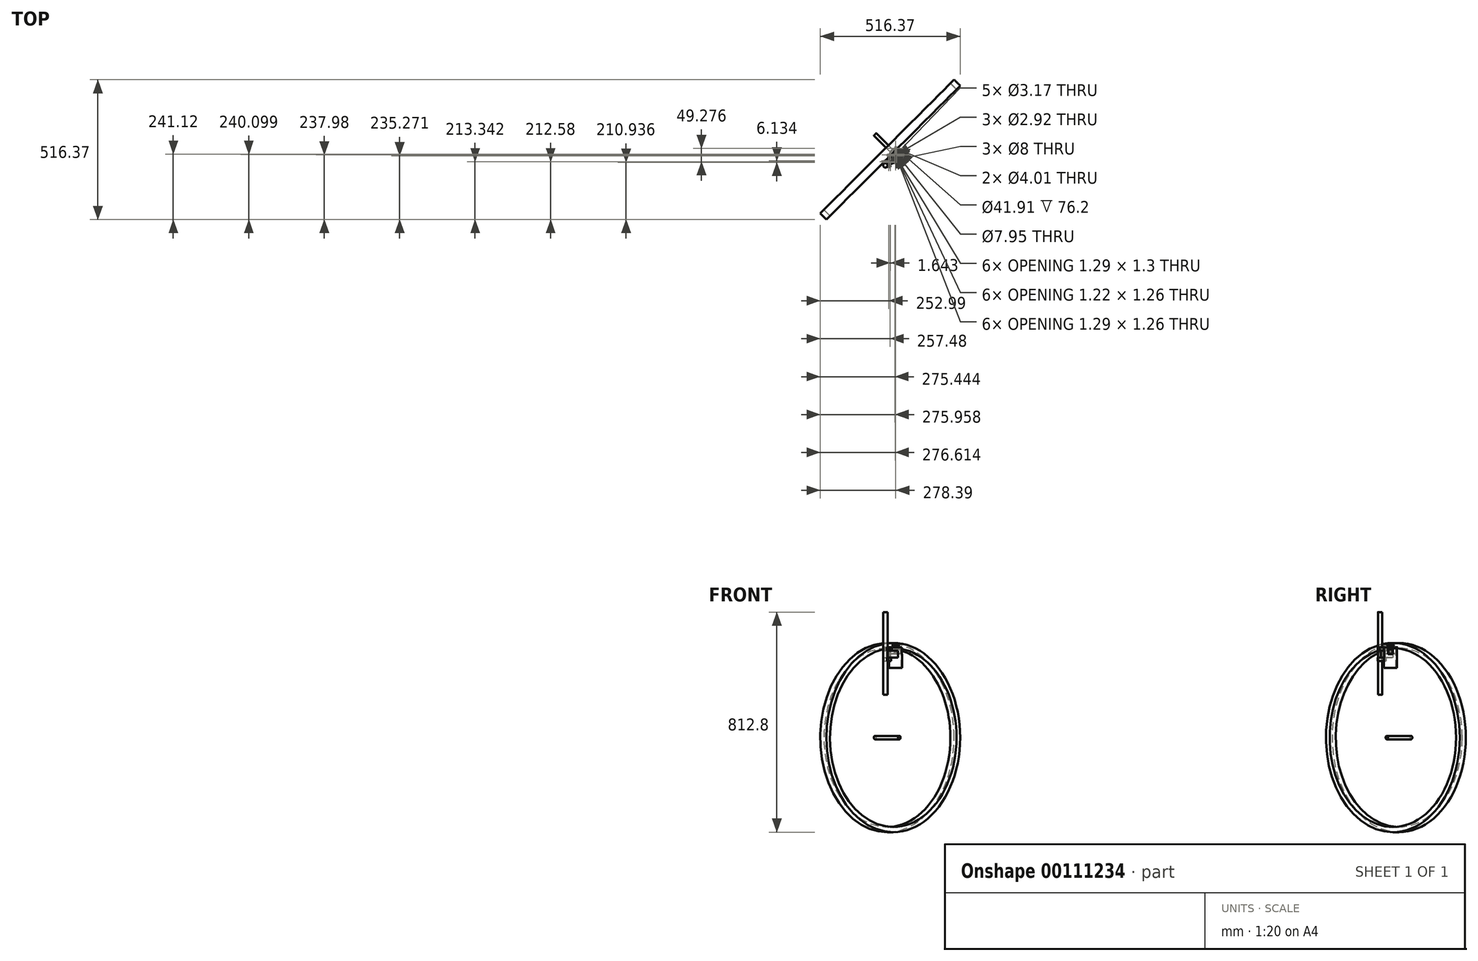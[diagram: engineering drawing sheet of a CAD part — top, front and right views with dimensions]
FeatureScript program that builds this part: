
annotation { "Feature Type Name" : "Feature", "Feature Type Description" : "" }
export const myFeature = defineFeature(function(context is Context, id is Id, definition is map)
    precondition{}
    {
        {
            var Q0;
            Q0=qCreatedBy(makeId("Top.planeOp"),FACE);
            var sketch = newSketch(context, id + "F0", { "sketchPlane" : qUnion([Q0])});
            skCircle(sketch, "E0", {"center": v(0, 0) * mm, "radius": 20.96 * mm});
            skSolve(sketch);
        }
        {
            var Q0;
            Q0=makeQuery(id+"F0.imprint","IMPRINT",FACE,{"disambiguationData":[TD([[makeQuery(id+"F0.imprint","IMPRINT",EDGE,{"derivedFrom":sQuery(id+"F0.wireOp",EDGE,"E0")}),1.0]])]});
            extrude(context, id + "F1", {"entities" : qUnion([Q0]), "depth" : 21.74 * mm});
        }
        {
            var Q0;
            Q0=makeQuery(id+"F1.opExtrude","CAP_FACE",FACE,{"disambiguationData":[OSD([sQuery(id+"F0.wireOp",EDGE,"E0")])],"isStart":false});
            var sketch = newSketch(context, id + "F2", { "sketchPlane" : qUnion([Q0])});
            skArc(sketch, "E1.0", {"start": v(15.25, -13.43) * mm, "mid": v(20.32, 0) * mm, "end": v(15.25, 13.43) * mm});
            skLineSegment(sketch, "E2", {"start": v(0, 32.45) * mm, "end": v(0, -32.45) * mm, "construction": true});
            skLineSegment(sketch, "E3", {"start": v(0, 0) * mm, "end": v(29.8, 0) * mm, "construction": true});
            skCircle(sketch, "E4", {"center": v(0, 24.64) * mm, "radius": 2 * mm});
            skCircle(sketch, "E5", {"center": v(0, -24.64) * mm, "radius": 2 * mm});
            skArc(sketch, "E6.0", {"start": v(3.03, 27.3) * mm, "mid": v(0, 28.68) * mm, "end": v(-3.03, 27.3) * mm});
            skArc(sketch, "E7", {"start": v(-3.03, -27.3) * mm, "mid": v(0, -28.68) * mm, "end": v(3.03, -27.3) * mm});
            skLineSegment(sketch, "E8", {"start": v(-3.03, 27.3) * mm, "end": v(-15.25, 13.43) * mm});
            skLineSegment(sketch, "E9", {"start": v(3.03, 27.3) * mm, "end": v(15.25, 13.43) * mm});
            skLineSegment(sketch, "E10", {"start": v(-3.03, -27.3) * mm, "end": v(-15.25, -13.43) * mm});
            skLineSegment(sketch, "E11", {"start": v(3.03, -27.3) * mm, "end": v(15.25, -13.43) * mm});
            skArc(sketch, "E12.trimOffspring", {"start": v(-15.25, 13.43) * mm, "mid": v(-20.32, 0) * mm, "end": v(-15.25, -13.43) * mm});
            skSolve(sketch);
        }
        {
            var Q0;
            Q0=makeQuery(id+"F2.imprint","IMPRINT",FACE,{"disambiguationData":[TD([[makeQuery(id+"F2.imprint","IMPRINT",EDGE,{"derivedFrom":sQuery(id+"F2.wireOp",EDGE,"E4")}),-1.0]])]});
            var Q1;
            {var subQ8=sQuery(id+"F2.wireOp",EDGE,"E1.0");Q1=makeQuery(id+"F2.imprint","IMPRINT",FACE,{"disambiguationData":[TD([[makeQuery(id+"F2.imprint","IMPRINT",EDGE,{"derivedFrom":subQ8}),1.0]])]});}
            var Q2;
            Q2=makeQuery(id+"F2.imprint","IMPRINT",FACE,{"disambiguationData":[TD([[makeQuery(id+"F2.imprint","IMPRINT",EDGE,{"derivedFrom":sQuery(id+"F2.wireOp",EDGE,"E5")}),-1.0]])]});
            extrude(context, id + "F3", {"entities" : qUnion([Q0, Q1, Q2]), "depth" : 0.76 * mm});
        }
        {
            var Q0;
            Q0=makeQuery(id+"F3.opExtrude","CAP_FACE",FACE,{"disambiguationData":[OSD([sQuery(id+"F2.wireOp",EDGE,"E1.0"),sQuery(id+"F2.wireOp",EDGE,"E4"),sQuery(id+"F2.wireOp",EDGE,"E5"),sQuery(id+"F2.wireOp",EDGE,"E6.0"),sQuery(id+"F2.wireOp",EDGE,"E7"),sQuery(id+"F2.wireOp",EDGE,"E8"),sQuery(id+"F2.wireOp",EDGE,"E9"),sQuery(id+"F2.wireOp",EDGE,"E10"),sQuery(id+"F2.wireOp",EDGE,"E11"),sQuery(id+"F2.wireOp",EDGE,"E12.trimOffspring")])],"isStart":false});
            var sketch = newSketch(context, id + "F4", { "sketchPlane" : qUnion([Q0])});
            skCircle(sketch, "E13", {"center": v(0, 0) * mm, "radius": 4.94 * mm});
            skCircle(sketch, "E14", {"center": v(0, 0) * mm, "radius": 1.46 * mm});
            skSolve(sketch);
        }
        {
            var Q0;
            Q0=makeQuery(id+"F4.imprint","IMPRINT",FACE,{"disambiguationData":[TD([[makeQuery(id+"F4.imprint","IMPRINT",EDGE,{"derivedFrom":sQuery(id+"F4.wireOp",EDGE,"E13")}),1.0]])]});
            extrude(context, id + "F5", {"entities" : qUnion([Q0]), "operationType" : NewBodyOperationType.ADD, "depth" : 1.4 * mm});
        }
        {
            var Q0;
            Q0=makeQuery(id+"F4.imprint","IMPRINT",FACE,{"disambiguationData":[TD([[makeQuery(id+"F4.imprint","IMPRINT",EDGE,{"derivedFrom":sQuery(id+"F4.wireOp",EDGE,"E14")}),1.0]])]});
            extrude(context, id + "F6", {"entities" : qUnion([Q0]), "operationType" : NewBodyOperationType.REMOVE, "endBound" : BoundingType.THROUGH_ALL, "oppositeDirection" : true, "depth" : 25.4 * mm});
        }
        {
            var Q0;
            Q0=makeQuery(id+"F5.opExtrude","CAP_FACE",FACE,{"disambiguationData":[OSD([sQuery(id+"F4.wireOp",EDGE,"E13"),sQuery(id+"F4.wireOp",EDGE,"E14")])],"isStart":false});
            var sketch = newSketch(context, id + "F7", { "sketchPlane" : qUnion([Q0])});
            skCircle(sketch, "E15.0", {"center": v(0, 0) * mm, "radius": 1.46 * mm});
            skSolve(sketch);
        }
        {
            var Q0;
            Q0 = qSketchRegion(id + "F7", true);
            var Q1;
            Q1=makeQuery(id+"F7.imprint","IMPRINT",FACE,{"disambiguationData":[TD([[makeQuery(id+"F7.imprint","IMPRINT",EDGE,{"derivedFrom":sQuery(id+"F7.wireOp",EDGE,"E15.0")}),1.0]])]});
            extrude(context, id + "F8", {"entities" : qUnion([Q0, Q1]), "depth" : 7.62 * mm, "hasSecondDirection" : true, "secondDirectionOppositeDirection" : true, "secondDirectionDepth" : 25.65 * mm});
        }
        {
            var Q0;
            Q0=makeQuery(id+"F1.opExtrude","CAP_FACE",FACE,{"disambiguationData":[OSD([sQuery(id+"F0.wireOp",EDGE,"E0")])],"isStart":true});
            var sketch = newSketch(context, id + "F9", { "sketchPlane" : qUnion([Q0])});
            skCircle(sketch, "E16", {"center": v(0, 0) * mm, "radius": 15.58 * mm});
            skSolve(sketch);
        }
        {
            var Q0;
            Q0 = qSketchRegion(id + "F9", true);
            extrude(context, id + "F10", {"entities" : qUnion([Q0]), "depth" : 1.68 * mm});
        }
        {
            var Q0;
            Q0=makeQuery(id+"F1.opExtrude","CAP_EDGE",EDGE,{"disambiguationData":[OSD([sQuery(id+"F0.wireOp",EDGE,"E0")])],"isStart":false});
            fillet(context, id + "F11", {"entities" : qUnion([Q0]), "radius" : 0.25 * mm, "tangentPropagation" : true, "allowEdgeOverflow" : false});
        }
        {
            var Q0;
            Q0=makeQuery(id+"F8.opExtrude","CAP_FACE",FACE,{"disambiguationData":[OSD([sQuery(id+"F7.wireOp",EDGE,"E15.0")])],"isStart":false});
            var sketch = newSketch(context, id + "F12", { "sketchPlane" : qUnion([Q0])});
            skCircle(sketch, "E17", {"center": v(0, 0) * mm, "radius": 3.98 * mm});
            skCircle(sketch, "E18.0", {"center": v(0, 0) * mm, "radius": 1.46 * mm});
            skSolve(sketch);
        }
        {
            var Q0;
            Q0=makeQuery(id+"F12.imprint","IMPRINT",FACE,{"disambiguationData":[TD([[makeQuery(id+"F12.imprint","IMPRINT",EDGE,{"derivedFrom":sQuery(id+"F12.wireOp",EDGE,"E17")}),1.0]])]});
            extrude(context, id + "F13", {"entities" : qUnion([Q0]), "oppositeDirection" : true, "depth" : 6.1 * mm});
        }
        {
            var Q0;
            Q0=qCreatedBy(makeId("Right.planeOp"),FACE);
            cPlane(context, id + "F14", {"entities" : qUnion([Q0]), "cplaneType" : CPlaneType.OFFSET, "offset" : 21.34 * mm, "width" : 152.4 * mm, "height" : 152.4 * mm});
        }
        {
            var Q0;
            Q0=qCreatedBy(id+"F14.planeOp",FACE);
            var sketch = newSketch(context, id + "F15", { "sketchPlane" : qUnion([Q0])});
            skLineSegment(sketch, "E19.bottom", {"start": v(7.96, -1.7) * mm, "end": v(-7.96, -1.7) * mm});
            skLineSegment(sketch, "E19.top", {"start": v(7.96, 14.99) * mm, "end": v(-7.96, 14.99) * mm});
            skLineSegment(sketch, "E19.left", {"start": v(7.96, -1.7) * mm, "end": v(7.96, 14.99) * mm});
            skLineSegment(sketch, "E19.right", {"start": v(-7.96, -1.7) * mm, "end": v(-7.96, 14.99) * mm});
            skPoint(sketch, "E19.middle", {"position": v(0, 6.64) * mm});
            skSolve(sketch);
        }
        {
            var Q0;
            Q0=makeQuery(id+"F15.imprint","IMPRINT",FACE,{"disambiguationData":[TD([[makeQuery(id+"F15.imprint","IMPRINT",EDGE,{"derivedFrom":sQuery(id+"F15.wireOp",EDGE,"E19.bottom")}),-1.0]])]});
            extrude(context, id + "F16", {"entities" : qUnion([Q0]), "depth" : 0.91 * mm});
        }
        {
            var Q0;
            Q0=makeQuery(id+"F16.opExtrude","SWEPT_EDGE",EDGE,{"disambiguationData":[OSD([sQuery(id+"F15.wireOp",EDGE,"E19.top"),sQuery(id+"F15.wireOp",EDGE,"E19.right")])]});
            chamfer(context, id + "F17", {"entities" : qUnion([Q0]), "width" : 1.27 * mm, "tangentPropagation" : true});
        }
        {
            var Q0;
            Q0=makeQuery(id+"F3.opExtrude","CAP_FACE",FACE,{"disambiguationData":[OSD([sQuery(id+"F2.wireOp",EDGE,"E1.0"),sQuery(id+"F2.wireOp",EDGE,"E4"),sQuery(id+"F2.wireOp",EDGE,"E5"),sQuery(id+"F2.wireOp",EDGE,"E6.0"),sQuery(id+"F2.wireOp",EDGE,"E7"),sQuery(id+"F2.wireOp",EDGE,"E8"),sQuery(id+"F2.wireOp",EDGE,"E9"),sQuery(id+"F2.wireOp",EDGE,"E10"),sQuery(id+"F2.wireOp",EDGE,"E11"),sQuery(id+"F2.wireOp",EDGE,"E12.trimOffspring")])],"isStart":true});
            var sketch = newSketch(context, id + "F18", { "sketchPlane" : qUnion([Q0])});
            skCircle(sketch, "E20.0", {"center": v(0, 0) * mm, "radius": 20.96 * mm});
            skCircle(sketch, "E21", {"center": v(0, 0) * mm, "radius": 24.13 * mm});
            skSolve(sketch);
        }
        {
            var Q0;
            Q0 = qSketchRegion(id + "F18", true);
            extrude(context, id + "F19", {"entities" : qUnion([Q0]), "depth" : 76.2 * mm});
        }
        {
            var Q0;
            Q0=makeQuery(id+"F16.opExtrude","CAP_FACE",FACE,{"disambiguationData":[OSD([sQuery(id+"F15.wireOp",EDGE,"E19.bottom"),sQuery(id+"F15.wireOp",EDGE,"E19.top"),sQuery(id+"F15.wireOp",EDGE,"E19.left"),sQuery(id+"F15.wireOp",EDGE,"E19.right")])],"isStart":false});
            var sketch = newSketch(context, id + "F20", { "sketchPlane" : qUnion([Q0])});
            skLineSegment(sketch, "E22.0", {"start": v(7.96, 14.99) * mm, "end": v(-6.7, 14.99) * mm, "construction": true});
            skLineSegment(sketch, "E23.0", {"start": v(7.96, -1.7) * mm, "end": v(7.96, 14.99) * mm, "construction": true});
            skLineSegment(sketch, "E24.0", {"start": v(7.96, -1.7) * mm, "end": v(-7.96, -1.7) * mm, "construction": true});
            skLineSegment(sketch, "E25.0", {"start": v(-7.96, -1.7) * mm, "end": v(-7.96, 13.72) * mm, "construction": true});
            skLineSegment(sketch, "E26.0", {"start": v(-6.7, 14.99) * mm, "end": v(-7.96, 13.72) * mm, "construction": true});
            skLineSegment(sketch, "E27", {"start": v(-7.96, -1.7) * mm, "end": v(7.96, 14.99) * mm, "construction": true});
            skLineSegment(sketch, "E28.bottom", {"start": v(8.57, -3.66) * mm, "end": v(-8.57, -3.66) * mm});
            skLineSegment(sketch, "E28.left", {"start": v(8.57, -3.66) * mm, "end": v(8.57, 21.74) * mm});
            skLineSegment(sketch, "E28.right", {"start": v(-8.57, -3.66) * mm, "end": v(-8.57, 21.74) * mm});
            skPoint(sketch, "E28.middle", {"position": v(0, 6.64) * mm});
            skLineSegment(sketch, "E29.0", {"start": v(8.57, 21.74) * mm, "end": v(-8.57, 21.74) * mm});
            skPoint(sketch, "E30.orphan", {"position": v(-8.57, 16.94) * mm});
            skPoint(sketch, "E31.orphan", {"position": v(8.57, 16.94) * mm});
            skPoint(sketch, "E32.orphan", {"position": v(-24.13, 21.74) * mm});
            skPoint(sketch, "E33.orphan", {"position": v(24.13, 21.74) * mm});
            skLineSegment(sketch, "E34", {"start": v(0, 6.64) * mm, "end": v(0, -8.32) * mm, "construction": true});
            skPoint(sketch, "E34.endSnap0", {"position": v(0, -3.66) * mm});
            skSolve(sketch);
        }
        {
            var Q0;
            Q0 = qSketchRegion(id + "F20", true);
            extrude(context, id + "F21", {"entities" : qUnion([Q0]), "endBound" : BoundingType.SYMMETRIC, "depth" : 25.4 * mm});
        }
        {
            var Q0;
            Q0=makeQuery(id+"F21.opExtrude","SWEPT_BODY",BODY,{"disambiguationData":[OSD([sQuery(id+"F20.wireOp",EDGE,"E28.bottom"),sQuery(id+"F20.wireOp",EDGE,"E28.left"),sQuery(id+"F20.wireOp",EDGE,"E28.right"),sQuery(id+"F20.wireOp",EDGE,"E29.0")])]});
            var Q1;
            Q1=makeQuery(id+"F19.opExtrude","SWEPT_BODY",BODY,{"disambiguationData":[OSD([sQuery(id+"F18.wireOp",EDGE,"E20.0"),sQuery(id+"F18.wireOp",EDGE,"E21")])]});
            booleanBodies(context, id + "F22", {"operationType" : BooleanOperationType.SUBTRACTION, "tools" : qUnion([Q0]), "targets" : qUnion([Q1])});
        }
        {
            var Q0;
            Q0=qCreatedBy(makeId("Top.planeOp"),FACE);
            var sketch = newSketch(context, id + "F23", { "sketchPlane" : qUnion([Q0])});
            skCircle(sketch, "E35", {"center": v(-38.1, -38.1) * mm, "radius": 7.94 * mm});
            skSolve(sketch);
        }
        {
            var Q0;
            Q0=makeQuery(id+"F23.imprint","IMPRINT",FACE,{"disambiguationData":[TD([[makeQuery(id+"F23.imprint","IMPRINT",EDGE,{"derivedFrom":sQuery(id+"F23.wireOp",EDGE,"E35")}),1.0]])]});
            extrude(context, id + "F24", {"entities" : qUnion([Q0]), "endBound" : BoundingType.SYMMETRIC, "depth" : 304.8 * mm});
        }
        {
            var Q0;
            Q0=makeQuery(id+"F19.opExtrude","CAP_FACE",FACE,{"disambiguationData":[OSD([sQuery(id+"F18.wireOp",EDGE,"E20.0"),sQuery(id+"F18.wireOp",EDGE,"E21")])],"isStart":true});
            var sketch = newSketch(context, id + "F25", { "sketchPlane" : qUnion([Q0])});
            skCircle(sketch, "E36", {"center": v(-25.4, -25.4) * mm, "radius": 4 * mm});
            skLineSegment(sketch, "E37", {"start": v(0, 0) * mm, "end": v(-25.4, -25.4) * mm, "construction": true});
            skSolve(sketch);
        }
        {
            var Q0;
            Q0=makeQuery(id+"F25.imprint","IMPRINT",FACE,{"disambiguationData":[TD([[makeQuery(id+"F25.imprint","IMPRINT",EDGE,{"derivedFrom":sQuery(id+"F25.wireOp",EDGE,"E36")}),1.0]])]});
            extrude(context, id + "F26", {"entities" : qUnion([Q0]), "oppositeDirection" : true, "depth" : 50.8 * mm});
        }
        {
            var Q0;
            Q0=makeQuery(id+"F26.opExtrude","CAP_FACE",FACE,{"disambiguationData":[OSD([sQuery(id+"F25.wireOp",EDGE,"E36")])],"isStart":true});
            var sketch = newSketch(context, id + "F27", { "sketchPlane" : qUnion([Q0])});
            skArc(sketch, "E38.0", {"start": v(-22.04, -27.57) * mm, "mid": v(-22.57, -22.57) * mm, "end": v(-27.57, -22.04) * mm, "construction": true});
            skLineSegment(sketch, "E39", {"start": v(-43.71, -32.49) * mm, "end": v(-27.57, -22.04) * mm, "construction": true});
            skLineSegment(sketch, "E40", {"start": v(-32.49, -43.71) * mm, "end": v(-22.04, -27.57) * mm, "construction": true});
            skLineSegment(sketch, "E41.0", {"start": v(-46.47, -28.22) * mm, "end": v(-30.33, -17.78) * mm});
            skLineSegment(sketch, "E41.2", {"start": v(-28.22, -46.47) * mm, "end": v(-17.78, -30.33) * mm});
            skArc(sketch, "E41.3", {"start": v(-17.78, -30.33) * mm, "mid": v(-18.98, -18.98) * mm, "end": v(-30.33, -17.78) * mm});
            skArc(sketch, "E42.0", {"start": v(-32.49, -43.71) * mm, "mid": v(-32.49, -32.49) * mm, "end": v(-43.71, -32.49) * mm});
            skLineSegment(sketch, "E43", {"start": v(-46.47, -28.22) * mm, "end": v(-43.71, -32.49) * mm});
            skLineSegment(sketch, "E44", {"start": v(-32.49, -43.71) * mm, "end": v(-28.22, -46.47) * mm});
            skLineSegment(sketch, "E45", {"start": v(-43.71, -32.49) * mm, "end": v(-32.49, -43.71) * mm, "construction": true});
            skLineSegment(sketch, "E46", {"start": v(-38.1, -38.1) * mm, "end": v(-25.4, -25.4) * mm, "construction": true});
            skCircle(sketch, "E47.0", {"center": v(-25.4, -25.4) * mm, "radius": 4 * mm});
            skSolve(sketch);
        }
        {
            var Q0;
            Q0=makeQuery(id+"F27.imprint","IMPRINT",FACE,{"disambiguationData":[TD([[makeQuery(id+"F27.imprint","IMPRINT",EDGE,{"derivedFrom":sQuery(id+"F27.wireOp",EDGE,"E41.0")}),-1.0]])]});
            extrude(context, id + "F28", {"entities" : qUnion([Q0]), "oppositeDirection" : true, "depth" : 12.7 * mm});
        }
        {
            var Q0;
            Q0=makeQuery(id+"F26.opExtrude","CAP_FACE",FACE,{"disambiguationData":[OSD([sQuery(id+"F25.wireOp",EDGE,"E36")])],"isStart":false});
            var sketch = newSketch(context, id + "F29", { "sketchPlane" : qUnion([Q0])});
            skLineSegment(sketch, "E48.0", {"start": v(-46.47, 28.22) * mm, "end": v(-30.33, 17.78) * mm});
            skLineSegment(sketch, "E49.0", {"start": v(-46.47, 28.22) * mm, "end": v(-43.71, 32.49) * mm});
            skArc(sketch, "E50.0", {"start": v(-43.71, 32.49) * mm, "mid": v(-32.49, 32.49) * mm, "end": v(-32.49, 43.71) * mm});
            skLineSegment(sketch, "E51.0", {"start": v(-32.49, 43.71) * mm, "end": v(-28.22, 46.47) * mm});
            skLineSegment(sketch, "E52.0", {"start": v(-28.22, 46.47) * mm, "end": v(-17.78, 30.33) * mm});
            skArc(sketch, "E53.0", {"start": v(-17.78, 30.33) * mm, "mid": v(-18.98, 18.98) * mm, "end": v(-30.33, 17.78) * mm});
            skCircle(sketch, "E54.0", {"center": v(-25.4, 25.4) * mm, "radius": 4 * mm});
            skSolve(sketch);
        }
        {
            var Q0;
            Q0=makeQuery(id+"F29.imprint","IMPRINT",FACE,{"disambiguationData":[TD([[makeQuery(id+"F29.imprint","IMPRINT",EDGE,{"derivedFrom":sQuery(id+"F29.wireOp",EDGE,"E48.0")}),1.0]])]});
            extrude(context, id + "F30", {"entities" : qUnion([Q0]), "oppositeDirection" : true, "depth" : 12.7 * mm});
        }
        {
            var Q0;
            Q0=makeQuery(id+"F28.opExtrude","SWEPT_FACE",FACE,{"disambiguationData":[OSD([sQuery(id+"F27.wireOp",EDGE,"E41.2")])]});
            var sketch = newSketch(context, id + "F31", { "sketchPlane" : qUnion([Q0])});
            skCircle(sketch, "E55", {"center": v(-48, 15.4) * mm, "radius": 1.59 * mm});
            skPoint(sketch, "E55.centerSnap0", {"position": v(-54.35, 15.4) * mm});
            skSolve(sketch);
        }
        {
            var Q0;
            Q0=makeQuery(id+"F31.imprint","IMPRINT",FACE,{"disambiguationData":[TD([[makeQuery(id+"F31.imprint","IMPRINT",EDGE,{"derivedFrom":sQuery(id+"F31.wireOp",EDGE,"E55")}),1.0]])]});
            extrude(context, id + "F32", {"entities" : qUnion([Q0]), "depth" : 3.17 * mm});
        }
        {
            var Q0;
            Q0=makeQuery(id+"F32.opExtrude","CAP_FACE",FACE,{"disambiguationData":[OSD([sQuery(id+"F31.wireOp",EDGE,"E55")])],"isStart":false});
            var sketch = newSketch(context, id + "F33", { "sketchPlane" : qUnion([Q0])});
            skCircle(sketch, "E56", {"center": v(-48, 15.4) * mm, "radius": 3.18 * mm});
            skSolve(sketch);
        }
        {
            var Q0;
            Q0=makeQuery(id+"F33.imprint","IMPRINT",FACE,{"disambiguationData":[TD([[makeQuery(id+"F33.imprint","IMPRINT",EDGE,{"derivedFrom":sQuery(id+"F33.wireOp",EDGE,"E56")}),1.0]])]});
            var Q1;
            Q1=makeQuery(id+"F33.imprint","IMPRINT",FACE,{"disambiguationData":[TD([[makeQuery(id+"F33.imprint","IMPRINT",EDGE,{"derivedFrom":makeQuery(id+"F32.opExtrude","CAP_EDGE",EDGE,{"disambiguationData":[OSD([sQuery(id+"F31.wireOp",EDGE,"E55")])],"isStart":false})}),1.0]])]});
            extrude(context, id + "F34", {"entities" : qUnion([Q0, Q1]), "operationType" : NewBodyOperationType.ADD, "depth" : 1.59 * mm});
        }
        {
            var Q0;
            Q0=qCreatedBy(makeId("Right.planeOp"),FACE);
            var Q1;
            Q1=qCreatedBy(makeId("Front.planeOp"),FACE);
            cPlane(context, id + "F35", {"entities" : qUnion([Q0, Q1]), "cplaneType" : CPlaneType.MID_PLANE, "offset" : 25.4 * mm, "flipAlignment" : true, "width" : 152.4 * mm, "height" : 152.4 * mm});
        }
        {
            var Q0;
            Q0=makeQuery(id+"F32.opExtrude","SWEPT_BODY",BODY,{"disambiguationData":[OSD([sQuery(id+"F31.wireOp",EDGE,"E55")])]});
            var Q1;
            Q1=makeQuery(id+"F34.opExtrude","SWEPT_BODY",BODY,{"disambiguationData":[OSD([sQuery(id+"F33.wireOp",EDGE,"E56")])]});
            var Q2;
            Q2=qCreatedBy(id+"F35.planeOp",FACE);
            mirror(context, id + "F36", {"operationType" : NewBodyOperationType.ADD, "entities" : qUnion([Q0, Q1]), "mirrorPlane" : qUnion([Q2])});
        }
        {
            var Q0;
            Q0=makeQuery(id+"F13.opExtrude","CAP_FACE",FACE,{"disambiguationData":[OSD([sQuery(id+"F12.wireOp",EDGE,"E17"),sQuery(id+"F12.wireOp",EDGE,"E18.0")])],"isStart":true});
            var sketch = newSketch(context, id + "F37", { "sketchPlane" : qUnion([Q0])});
            skLineSegment(sketch, "E57", {"start": v(0, 3.47) * mm, "end": v(0, 5.27) * mm, "construction": true});
            skCircle(sketch, "E58.0", {"center": v(0, 0) * mm, "radius": 3.98 * mm});
            skLineSegment(sketch, "E59", {"start": v(0.64, 3.92) * mm, "end": v(0.24, 2.96) * mm});
            skLineSegment(sketch, "E60", {"start": v(0.24, 2.96) * mm, "end": v(0, 2.96) * mm});
            skLineSegment(sketch, "E61.MirrorCS", {"start": v(-0.24, 2.96) * mm, "end": v(0, 2.96) * mm});
            skLineSegment(sketch, "E62.MirrorCS", {"start": v(-0.64, 3.92) * mm, "end": v(-0.24, 2.96) * mm});
            skLineSegment(sketch, "E63.1.0", {"start": v(1.61, 3.07) * mm, "end": v(2.45, 4.66) * mm, "construction": true});
            skLineSegment(sketch, "E63.1.1", {"start": v(1.17, 2.73) * mm, "end": v(1.38, 2.62) * mm});
            skLineSegment(sketch, "E63.1.2", {"start": v(1.58, 2.51) * mm, "end": v(1.38, 2.62) * mm});
            skLineSegment(sketch, "E63.1.3", {"start": v(1.26, 3.77) * mm, "end": v(1.17, 2.73) * mm});
            skLineSegment(sketch, "E63.1.4", {"start": v(2.39, 3.18) * mm, "end": v(1.58, 2.51) * mm});
            skLineSegment(sketch, "E63.2.0", {"start": v(2.85, 1.97) * mm, "end": v(4.34, 3) * mm, "construction": true});
            skLineSegment(sketch, "E63.2.1", {"start": v(2.3, 1.87) * mm, "end": v(2.44, 1.68) * mm});
            skLineSegment(sketch, "E63.2.2", {"start": v(2.57, 1.49) * mm, "end": v(2.44, 1.68) * mm});
            skLineSegment(sketch, "E63.2.3", {"start": v(2.87, 2.75) * mm, "end": v(2.3, 1.87) * mm});
            skLineSegment(sketch, "E63.2.4", {"start": v(3.6, 1.7) * mm, "end": v(2.57, 1.49) * mm});
            skLineSegment(sketch, "E63.3.0", {"start": v(3.44, 0.42) * mm, "end": v(5.23, 0.63) * mm, "construction": true});
            skLineSegment(sketch, "E63.3.1", {"start": v(2.9, 0.6) * mm, "end": v(2.94, 0.36) * mm});
            skLineSegment(sketch, "E63.3.2", {"start": v(2.97, 0.12) * mm, "end": v(2.94, 0.36) * mm});
            skLineSegment(sketch, "E63.3.3", {"start": v(3.82, 1.1) * mm, "end": v(2.9, 0.6) * mm});
            skLineSegment(sketch, "E63.3.4", {"start": v(3.97, -0.16) * mm, "end": v(2.97, 0.12) * mm});
            skLineSegment(sketch, "E63.4.0", {"start": v(3.24, -1.23) * mm, "end": v(4.93, -1.87) * mm, "construction": true});
            skLineSegment(sketch, "E63.4.1", {"start": v(2.85, -0.83) * mm, "end": v(2.77, -1.05) * mm});
            skLineSegment(sketch, "E63.4.2", {"start": v(2.68, -1.27) * mm, "end": v(2.77, -1.05) * mm});
            skLineSegment(sketch, "E63.4.3", {"start": v(3.9, -0.8) * mm, "end": v(2.85, -0.83) * mm});
            skLineSegment(sketch, "E63.4.4", {"start": v(3.44, -1.99) * mm, "end": v(2.68, -1.27) * mm});
            skLineSegment(sketch, "E63.5.0", {"start": v(2.3, -2.6) * mm, "end": v(3.5, -3.94) * mm, "construction": true});
            skLineSegment(sketch, "E63.5.1", {"start": v(2.14, -2.06) * mm, "end": v(1.96, -2.21) * mm});
            skLineSegment(sketch, "E63.5.2", {"start": v(1.79, -2.37) * mm, "end": v(1.96, -2.21) * mm});
            skLineSegment(sketch, "E63.5.3", {"start": v(3.08, -2.52) * mm, "end": v(2.14, -2.06) * mm});
            skLineSegment(sketch, "E63.5.4", {"start": v(2.13, -3.36) * mm, "end": v(1.79, -2.37) * mm});
            skLineSegment(sketch, "E63.6.0", {"start": v(0.83, -3.37) * mm, "end": v(1.26, -5.11) * mm, "construction": true});
            skLineSegment(sketch, "E63.6.1", {"start": v(0.94, -2.82) * mm, "end": v(0.7, -2.87) * mm});
            skLineSegment(sketch, "E63.6.2", {"start": v(0.48, -2.93) * mm, "end": v(0.7, -2.87) * mm});
            skLineSegment(sketch, "E63.6.3", {"start": v(1.56, -3.66) * mm, "end": v(0.94, -2.82) * mm});
            skLineSegment(sketch, "E63.6.4", {"start": v(0.32, -3.96) * mm, "end": v(0.48, -2.93) * mm});
            skLineSegment(sketch, "E63.7.0", {"start": v(-0.83, -3.37) * mm, "end": v(-1.26, -5.11) * mm, "construction": true});
            skLineSegment(sketch, "E63.7.1", {"start": v(-0.48, -2.93) * mm, "end": v(-0.7, -2.87) * mm});
            skLineSegment(sketch, "E63.7.2", {"start": v(-0.94, -2.82) * mm, "end": v(-0.7, -2.87) * mm});
            skLineSegment(sketch, "E63.7.3", {"start": v(-0.32, -3.96) * mm, "end": v(-0.48, -2.93) * mm});
            skLineSegment(sketch, "E63.7.4", {"start": v(-1.56, -3.66) * mm, "end": v(-0.94, -2.82) * mm});
            skLineSegment(sketch, "E63.8.0", {"start": v(-2.3, -2.6) * mm, "end": v(-3.5, -3.94) * mm, "construction": true});
            skLineSegment(sketch, "E63.8.1", {"start": v(-1.79, -2.37) * mm, "end": v(-1.96, -2.21) * mm});
            skLineSegment(sketch, "E63.8.2", {"start": v(-2.14, -2.06) * mm, "end": v(-1.96, -2.21) * mm});
            skLineSegment(sketch, "E63.8.3", {"start": v(-2.13, -3.36) * mm, "end": v(-1.79, -2.37) * mm});
            skLineSegment(sketch, "E63.8.4", {"start": v(-3.08, -2.52) * mm, "end": v(-2.14, -2.06) * mm});
            skLineSegment(sketch, "E63.9.0", {"start": v(-3.24, -1.23) * mm, "end": v(-4.93, -1.87) * mm, "construction": true});
            skLineSegment(sketch, "E63.9.1", {"start": v(-2.68, -1.27) * mm, "end": v(-2.77, -1.05) * mm});
            skLineSegment(sketch, "E63.9.2", {"start": v(-2.85, -0.83) * mm, "end": v(-2.77, -1.05) * mm});
            skLineSegment(sketch, "E63.9.3", {"start": v(-3.44, -1.99) * mm, "end": v(-2.68, -1.27) * mm});
            skLineSegment(sketch, "E63.9.4", {"start": v(-3.9, -0.8) * mm, "end": v(-2.85, -0.83) * mm});
            skLineSegment(sketch, "E63.10.0", {"start": v(-3.44, 0.42) * mm, "end": v(-5.23, 0.63) * mm, "construction": true});
            skLineSegment(sketch, "E63.10.1", {"start": v(-2.97, 0.12) * mm, "end": v(-2.94, 0.36) * mm});
            skLineSegment(sketch, "E63.10.2", {"start": v(-2.9, 0.6) * mm, "end": v(-2.94, 0.36) * mm});
            skLineSegment(sketch, "E63.10.3", {"start": v(-3.97, -0.16) * mm, "end": v(-2.97, 0.12) * mm});
            skLineSegment(sketch, "E63.10.4", {"start": v(-3.82, 1.1) * mm, "end": v(-2.9, 0.6) * mm});
            skLineSegment(sketch, "E63.11.0", {"start": v(-2.85, 1.97) * mm, "end": v(-4.34, 3) * mm, "construction": true});
            skLineSegment(sketch, "E63.11.1", {"start": v(-2.57, 1.49) * mm, "end": v(-2.44, 1.68) * mm});
            skLineSegment(sketch, "E63.11.2", {"start": v(-2.3, 1.87) * mm, "end": v(-2.44, 1.68) * mm});
            skLineSegment(sketch, "E63.11.3", {"start": v(-3.6, 1.7) * mm, "end": v(-2.57, 1.49) * mm});
            skLineSegment(sketch, "E63.11.4", {"start": v(-2.87, 2.75) * mm, "end": v(-2.3, 1.87) * mm});
            skLineSegment(sketch, "E63.12.0", {"start": v(-1.61, 3.07) * mm, "end": v(-2.45, 4.66) * mm, "construction": true});
            skLineSegment(sketch, "E63.12.1", {"start": v(-1.58, 2.51) * mm, "end": v(-1.38, 2.62) * mm});
            skLineSegment(sketch, "E63.12.2", {"start": v(-1.17, 2.73) * mm, "end": v(-1.38, 2.62) * mm});
            skLineSegment(sketch, "E63.12.3", {"start": v(-2.39, 3.18) * mm, "end": v(-1.58, 2.51) * mm});
            skLineSegment(sketch, "E63.12.4", {"start": v(-1.26, 3.77) * mm, "end": v(-1.17, 2.73) * mm});
            skLineSegment(sketch, "E63.13.4", {"start": v(0.63, 3.92) * mm, "end": v(0.24, 2.96) * mm});
            skSolve(sketch);
        }
        {
            var Q0;
            Q0=makeQuery(id+"F37.imprint","IMPRINT",FACE,{"disambiguationData":[TD([[makeQuery(id+"F37.imprint","IMPRINT",EDGE,{"derivedFrom":sQuery(id+"F37.wireOp",EDGE,"E61.MirrorCS")}),1.0]])]});
            var Q1;
            Q1=makeQuery(id+"F37.imprint","IMPRINT",FACE,{"disambiguationData":[TD([[makeQuery(id+"F37.imprint","IMPRINT",EDGE,{"derivedFrom":sQuery(id+"F37.wireOp",EDGE,"E63.2.1")}),1.0]])]});
            var Q2;
            Q2=makeQuery(id+"F37.imprint","IMPRINT",FACE,{"disambiguationData":[TD([[makeQuery(id+"F37.imprint","IMPRINT",EDGE,{"derivedFrom":sQuery(id+"F37.wireOp",EDGE,"E63.1.1")}),1.0]])]});
            var Q3;
            Q3=makeQuery(id+"F37.imprint","IMPRINT",FACE,{"disambiguationData":[TD([[makeQuery(id+"F37.imprint","IMPRINT",EDGE,{"derivedFrom":sQuery(id+"F37.wireOp",EDGE,"E63.3.1")}),1.0]])]});
            var Q4;
            Q4=makeQuery(id+"F37.imprint","IMPRINT",FACE,{"disambiguationData":[TD([[makeQuery(id+"F37.imprint","IMPRINT",EDGE,{"derivedFrom":sQuery(id+"F37.wireOp",EDGE,"E63.4.1")}),1.0]])]});
            var Q5;
            Q5=makeQuery(id+"F37.imprint","IMPRINT",FACE,{"disambiguationData":[TD([[makeQuery(id+"F37.imprint","IMPRINT",EDGE,{"derivedFrom":sQuery(id+"F37.wireOp",EDGE,"E63.5.1")}),1.0]])]});
            var Q6;
            Q6=makeQuery(id+"F37.imprint","IMPRINT",FACE,{"disambiguationData":[TD([[makeQuery(id+"F37.imprint","IMPRINT",EDGE,{"derivedFrom":sQuery(id+"F37.wireOp",EDGE,"E63.6.1")}),1.0]])]});
            var Q7;
            Q7=makeQuery(id+"F37.imprint","IMPRINT",FACE,{"disambiguationData":[TD([[makeQuery(id+"F37.imprint","IMPRINT",EDGE,{"derivedFrom":sQuery(id+"F37.wireOp",EDGE,"E63.7.1")}),1.0]])]});
            var Q8;
            Q8=makeQuery(id+"F37.imprint","IMPRINT",FACE,{"disambiguationData":[TD([[makeQuery(id+"F37.imprint","IMPRINT",EDGE,{"derivedFrom":sQuery(id+"F37.wireOp",EDGE,"E63.9.1")}),1.0]])]});
            var Q9;
            Q9=makeQuery(id+"F37.imprint","IMPRINT",FACE,{"disambiguationData":[TD([[makeQuery(id+"F37.imprint","IMPRINT",EDGE,{"derivedFrom":sQuery(id+"F37.wireOp",EDGE,"E63.10.1")}),1.0]])]});
            var Q10;
            Q10=makeQuery(id+"F37.imprint","IMPRINT",FACE,{"disambiguationData":[TD([[makeQuery(id+"F37.imprint","IMPRINT",EDGE,{"derivedFrom":sQuery(id+"F37.wireOp",EDGE,"E63.11.1")}),1.0]])]});
            var Q11;
            Q11=makeQuery(id+"F37.imprint","IMPRINT",FACE,{"disambiguationData":[TD([[makeQuery(id+"F37.imprint","IMPRINT",EDGE,{"derivedFrom":sQuery(id+"F37.wireOp",EDGE,"E63.12.1")}),1.0]])]});
            var Q12;
            Q12=makeQuery(id+"F37.imprint","IMPRINT",FACE,{"disambiguationData":[TD([[makeQuery(id+"F37.imprint","IMPRINT",EDGE,{"derivedFrom":sQuery(id+"F37.wireOp",EDGE,"E63.8.1")}),1.0]])]});
            extrude(context, id + "F38", {"entities" : qUnion([Q0, Q1, Q2, Q3, Q4, Q5, Q6, Q7, Q8, Q9, Q10, Q11, Q12]), "operationType" : NewBodyOperationType.REMOVE, "endBound" : BoundingType.THROUGH_ALL, "oppositeDirection" : true, "depth" : 25.4 * mm});
        }
        {
            var Q0;
            Q0=makeQuery(id+"F13.opExtrude","CAP_FACE",FACE,{"disambiguationData":[OSD([sQuery(id+"F12.wireOp",EDGE,"E17"),sQuery(id+"F12.wireOp",EDGE,"E18.0")])],"isStart":true});
            var sketch = newSketch(context, id + "F39", { "sketchPlane" : qUnion([Q0])});
            skCircle(sketch, "E64", {"center": v(0, 0) * mm, "radius": 11.11 * mm});
            skCircle(sketch, "E65", {"center": v(0, 0) * mm, "radius": 6.35 * mm});
            skCircle(sketch, "E66", {"center": v(0, 0) * mm, "radius": 3.98 * mm});
            skSolve(sketch);
        }
        {
            var Q0;
            Q0=makeQuery(id+"F39.imprint","IMPRINT",FACE,{"disambiguationData":[TD([[makeQuery(id+"F39.imprint","IMPRINT",EDGE,{"derivedFrom":sQuery(id+"F39.wireOp",EDGE,"E65")}),1.0]])]});
            var Q1;
            Q1=makeQuery(id+"F39.imprint","IMPRINT",FACE,{"disambiguationData":[TD([[makeQuery(id+"F39.imprint","IMPRINT",EDGE,{"derivedFrom":sQuery(id+"F39.wireOp",EDGE,"E64")}),1.0]])]});
            extrude(context, id + "F40", {"entities" : qUnion([Q0, Q1]), "oppositeDirection" : true, "depth" : 3.17 * mm});
        }
        {
            var Q0;
            Q0=qCreatedBy(makeId("Right.planeOp"),FACE);
            var sketch = newSketch(context, id + "F41", { "sketchPlane" : qUnion([Q0])});
            skCircle(sketch, "E67", {"center": v(11.11, 29.93) * mm, "radius": 1.27 * mm});
            skLineSegment(sketch, "E68", {"start": v(11.11, 31.52) * mm, "end": v(11.11, 28.35) * mm, "construction": true});
            skSolve(sketch);
        }
        {
            var Q0;
            Q0=makeQuery(id+"F41.imprint","IMPRINT",FACE,{"disambiguationData":[TD([[makeQuery(id+"F41.imprint","IMPRINT",EDGE,{"derivedFrom":sQuery(id+"F41.wireOp",EDGE,"E67")}),1.0]])]});
            var Q1;
            Q1=sQuery(id+"F39.wireOp",EDGE,"E64");
            revolve(context, id + "F42", {"operationType" : NewBodyOperationType.REMOVE, "entities" : qUnion([Q0]), "axis" : qUnion([Q1]), "revolveType" : RevolveType.FULL, "oppositeDirection" : true});
        }
        {
            var Q0;
            Q0=makeQuery(id+"F41.imprint","IMPRINT",FACE,{"disambiguationData":[TD([[makeQuery(id+"F41.imprint","IMPRINT",EDGE,{"derivedFrom":sQuery(id+"F41.wireOp",EDGE,"E67")}),1.0]])]});
            var Q1;
            Q1=sQuery(id+"F39.wireOp",EDGE,"E64");
            revolve(context, id + "F43", {"entities" : qUnion([Q0]), "axis" : qUnion([Q1]), "revolveType" : RevolveType.FULL});
        }
        {
            var Q0;
            Q0=qCreatedBy(id+"F35.planeOp",FACE);
            cPlane(context, id + "F44", {"entities" : qUnion([Q0]), "cplaneType" : CPlaneType.OFFSET, "offset" : 44.45 * mm, "oppositeDirection" : true, "width" : 152.4 * mm, "height" : 152.4 * mm});
        }
        {
            var Q0;
            Q0=qCreatedBy(makeId("Top.planeOp"),FACE);
            var sketch = newSketch(context, id + "F45", { "sketchPlane" : qUnion([Q0])});
            skCircle(sketch, "E69.0", {"center": v(-25.4, -25.4) * mm, "radius": 4 * mm});
            skArc(sketch, "E70.0", {"start": v(-34.3, -21.99) * mm, "mid": v(-32.14, -32.14) * mm, "end": v(-21.99, -34.3) * mm});
            skArc(sketch, "E71.0", {"start": v(8.65, -22.53) * mm, "mid": v(-17.06, -17.06) * mm, "end": v(-22.53, 8.65) * mm});
            skLineSegment(sketch, "E72", {"start": v(-34.3, -21.99) * mm, "end": v(-22.53, 8.65) * mm});
            skLineSegment(sketch, "E73", {"start": v(-21.99, -34.3) * mm, "end": v(8.65, -22.53) * mm});
            skPoint(sketch, "E74.orphan", {"position": v(22.56, 8.57) * mm});
            skPoint(sketch, "E75.orphan", {"position": v(22.56, -8.57) * mm});
            skSolve(sketch);
        }
        {
            var Q0;
            Q0=makeQuery(id+"F45.imprint","IMPRINT",FACE,{"disambiguationData":[TD([[makeQuery(id+"F45.imprint","IMPRINT",EDGE,{"derivedFrom":sQuery(id+"F45.wireOp",EDGE,"E69.0")}),-1.0]])]});
            var Q1;
            Q1=makeQuery(id+"F28.opExtrude","CAP_FACE",FACE,{"disambiguationData":[OSD([sQuery(id+"F27.wireOp",EDGE,"E41.0"),sQuery(id+"F27.wireOp",EDGE,"E41.2"),sQuery(id+"F27.wireOp",EDGE,"E41.3"),sQuery(id+"F27.wireOp",EDGE,"E42.0"),sQuery(id+"F27.wireOp",EDGE,"E43"),sQuery(id+"F27.wireOp",EDGE,"E44"),sQuery(id+"F27.wireOp",EDGE,"E47.0")])],"isStart":false});
            var Q2;
            Q2=makeQuery(id+"F30.opExtrude","CAP_FACE",FACE,{"disambiguationData":[OSD([sQuery(id+"F29.wireOp",EDGE,"E48.0"),sQuery(id+"F29.wireOp",EDGE,"E49.0"),sQuery(id+"F29.wireOp",EDGE,"E50.0"),sQuery(id+"F29.wireOp",EDGE,"E51.0"),sQuery(id+"F29.wireOp",EDGE,"E52.0"),sQuery(id+"F29.wireOp",EDGE,"E53.0"),sQuery(id+"F29.wireOp",EDGE,"E54.0")])],"isStart":false});
            extrude(context, id + "F46", {"entities" : qUnion([Q0]), "endBound" : BoundingType.UP_TO_SURFACE, "endBoundEntityFace" : qUnion([Q1]), "depth" : 7.11 * mm, "hasSecondDirection" : true, "secondDirectionBound" : SecondDirectionBoundingType.UP_TO_SURFACE, "secondDirectionOppositeDirection" : true, "secondDirectionBoundEntityFace" : qUnion([Q2]), "secondDirectionDepth" : 25.4 * mm});
        }
        {
            var Q0;
            Q0=qCreatedBy(id+"F44.planeOp",FACE);
            var sketch = newSketch(context, id + "F47", { "sketchPlane" : qUnion([Q0])});
            skCircle(sketch, "E76", {"center": v(0, -311.15) * mm, "radius": 330.2 * mm});
            skCircle(sketch, "E77.0", {"center": v(0, -311.15) * mm, "radius": 349.25 * mm});
            skLineSegment(sketch, "E78", {"start": v(0, -311.15) * mm, "end": v(0, 135.58) * mm, "construction": true});
            skLineSegment(sketch, "E79.0", {"start": v(24.13, 21.74) * mm, "end": v(-24.13, 21.74) * mm, "construction": true});
            skSolve(sketch);
        }
        {
            var Q0;
            Q0=makeQuery(id+"F47.imprint","IMPRINT",FACE,{"disambiguationData":[TD([[makeQuery(id+"F47.imprint","IMPRINT",EDGE,{"derivedFrom":sQuery(id+"F47.wireOp",EDGE,"E76")}),-1.0]])]});
            extrude(context, id + "F48", {"entities" : qUnion([Q0]), "depth" : 31.75 * mm});
        }
        {
            var Q0;
            Q0=qCreatedBy(id+"F44.planeOp",FACE);
            var sketch = newSketch(context, id + "F49", { "sketchPlane" : qUnion([Q0])});
            skCircle(sketch, "E80", {"center": v(0, -311.15) * mm, "radius": 6.35 * mm});
            skSolve(sketch);
        }
        {
            var Q0;
            Q0=makeQuery(id+"F49.imprint","IMPRINT",FACE,{"disambiguationData":[TD([[makeQuery(id+"F49.imprint","IMPRINT",EDGE,{"derivedFrom":sQuery(id+"F49.wireOp",EDGE,"E80")}),1.0]])]});
            extrude(context, id + "F50", {"entities" : qUnion([Q0]), "endBound" : BoundingType.SYMMETRIC, "depth" : 127 * mm});
        }
        {
            var Q0;
            Q0=makeQuery(id+"F28.opExtrude","CAP_FACE",FACE,{"disambiguationData":[OSD([sQuery(id+"F27.wireOp",EDGE,"E41.0"),sQuery(id+"F27.wireOp",EDGE,"E41.2"),sQuery(id+"F27.wireOp",EDGE,"E41.3"),sQuery(id+"F27.wireOp",EDGE,"E42.0"),sQuery(id+"F27.wireOp",EDGE,"E43"),sQuery(id+"F27.wireOp",EDGE,"E44"),sQuery(id+"F27.wireOp",EDGE,"E47.0")])],"isStart":true});
            var sketch = newSketch(context, id + "F51", { "sketchPlane" : qUnion([Q0])});
            skCircle(sketch, "E81", {"center": v(-20.9, -20.9) * mm, "radius": 1.59 * mm});
            skCircle(sketch, "E82", {"center": v(-25.4, -25.4) * mm, "radius": 6.35 * mm, "construction": true});
            skLineSegment(sketch, "E83", {"start": v(-25.4, -25.4) * mm, "end": v(-20.9, -20.9) * mm, "construction": true});
            skSolve(sketch);
        }
        {
            var Q0;
            Q0=makeQuery(id+"F51.imprint","IMPRINT",FACE,{"disambiguationData":[TD([[makeQuery(id+"F51.imprint","IMPRINT",EDGE,{"derivedFrom":sQuery(id+"F51.wireOp",EDGE,"E81")}),1.0]])]});
            extrude(context, id + "F52", {"entities" : qUnion([Q0]), "operationType" : NewBodyOperationType.REMOVE, "endBound" : BoundingType.THROUGH_ALL, "oppositeDirection" : true, "depth" : 25.4 * mm});
        }
        {
            var Q0;
            Q0=makeQuery(id+"F46.opExtrude","CAP_FACE",FACE,{"disambiguationData":[OSD([sQuery(id+"F45.wireOp",EDGE,"E69.0"),sQuery(id+"F45.wireOp",EDGE,"E70.0"),sQuery(id+"F45.wireOp",EDGE,"E71.0"),sQuery(id+"F45.wireOp",EDGE,"E72"),sQuery(id+"F45.wireOp",EDGE,"E73")])],"isStart":false});
            var sketch = newSketch(context, id + "F53", { "sketchPlane" : qUnion([Q0])});
            skCircle(sketch, "E84", {"center": v(-25.4, -25.4) * mm, "radius": 6.35 * mm, "construction": true});
            skCircle(sketch, "E85", {"center": v(-19.27, -27.04) * mm, "radius": 1.59 * mm});
            skLineSegment(sketch, "E86", {"start": v(-25.4, -25.4) * mm, "end": v(-19.27, -27.04) * mm, "construction": true});
            skSolve(sketch);
        }
        {
            var Q0;
            Q0 = qSketchRegion(id + "F53", true);
            extrude(context, id + "F54", {"entities" : qUnion([Q0]), "operationType" : NewBodyOperationType.REMOVE, "endBound" : BoundingType.THROUGH_ALL, "oppositeDirection" : true, "depth" : 25.4 * mm});
        }
    });
